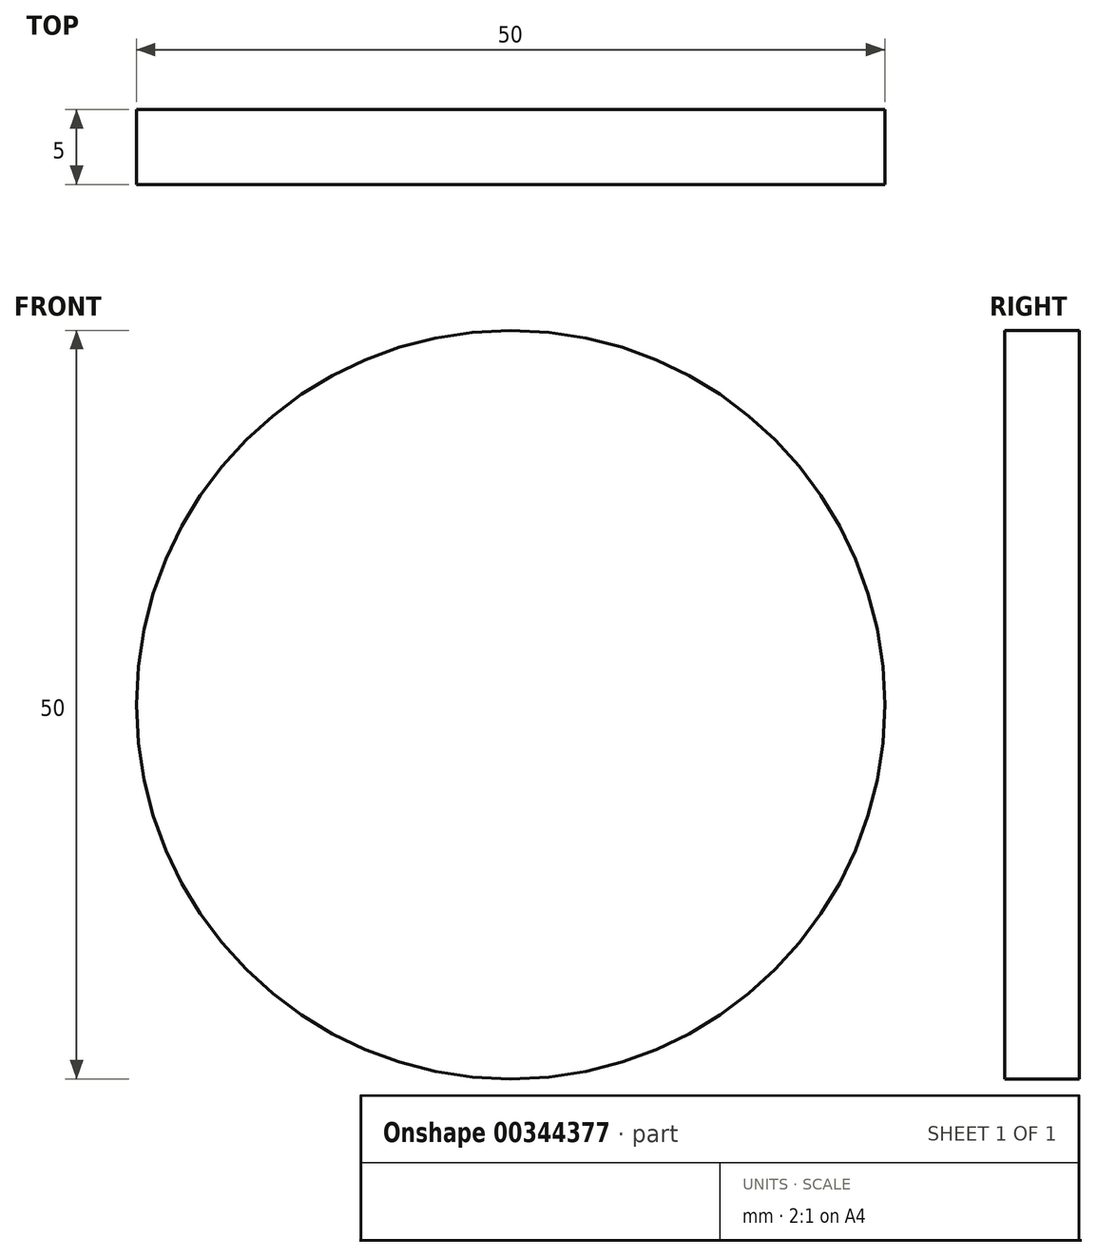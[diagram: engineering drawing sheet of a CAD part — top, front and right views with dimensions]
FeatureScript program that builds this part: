
annotation { "Feature Type Name" : "Feature", "Feature Type Description" : "" }
export const myFeature = defineFeature(function(context is Context, id is Id, definition is map)
    precondition{}
    {
        {
            var Q0;
            Q0=qCreatedBy(makeId("Front.planeOp"),FACE);
            var sketch = newSketch(context, id + "F0", { "sketchPlane" : qUnion([Q0])});
            skCircle(sketch, "E0", {"center": v(0, 14) * mm, "radius": 25 * mm});
            skSolve(sketch);
        }
        {
            var Q0;
            Q0=makeQuery(id+"F0.imprint","IMPRINT",FACE,{"disambiguationData":[TD([[makeQuery(id+"F0.imprint","IMPRINT",EDGE,{"derivedFrom":sQuery(id+"F0.wireOp",EDGE,"E0")}),1.0]])]});
            extrude(context, id + "F1", {"entities" : qUnion([Q0]), "depth" : -5 * mm});
        }
    });
